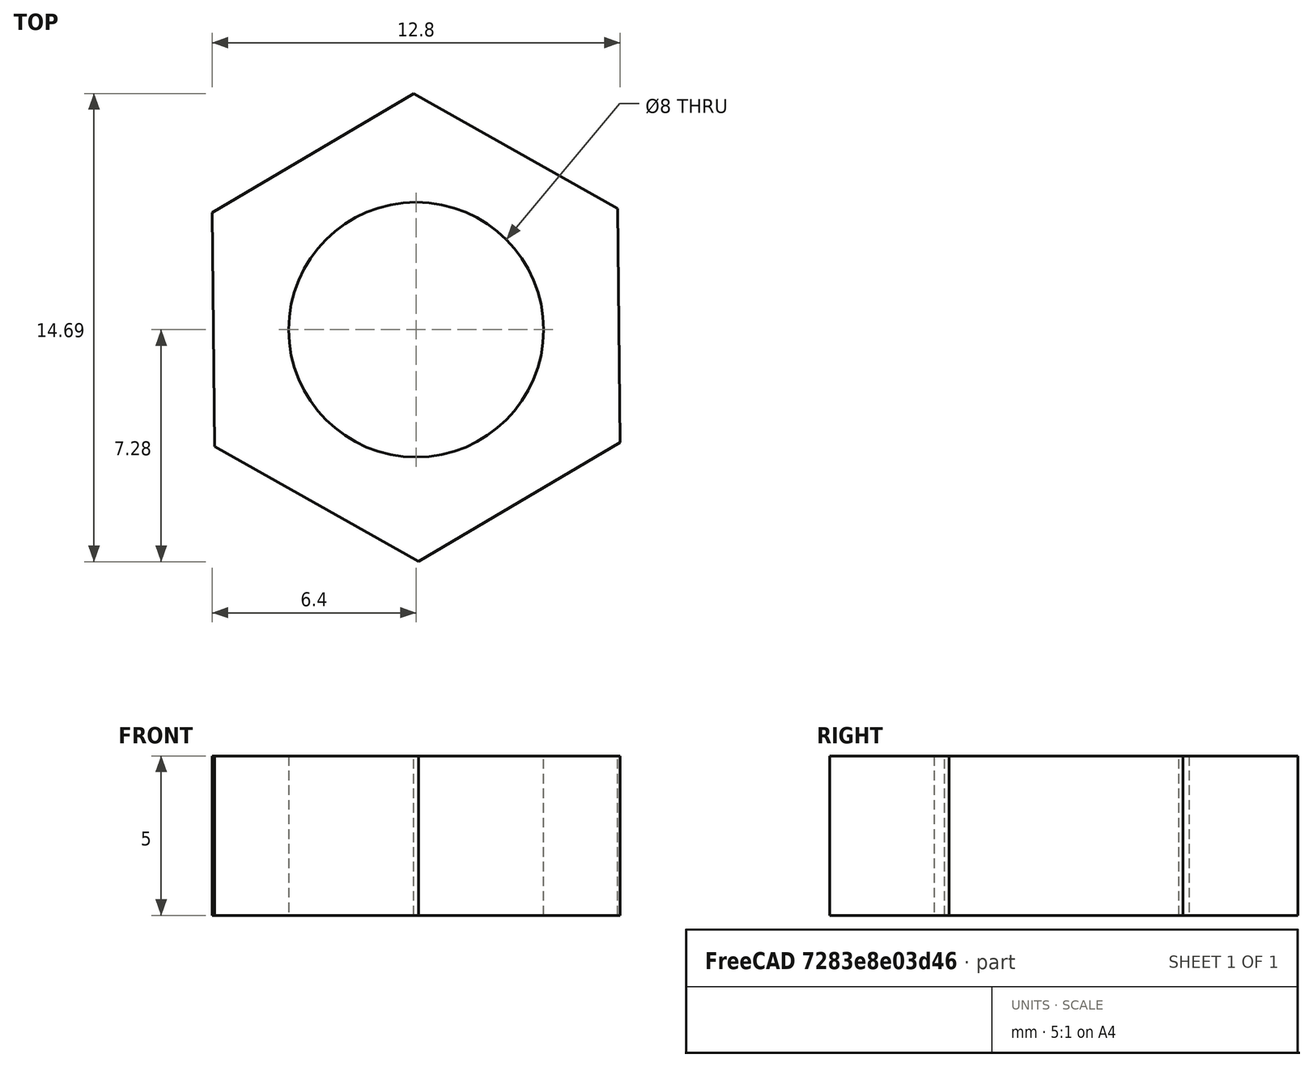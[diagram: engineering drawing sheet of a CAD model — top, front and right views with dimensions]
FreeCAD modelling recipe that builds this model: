
FCSTD DOCUMENT  (FreeCAD 0.19R24276 (Git))
Label: M8x5_gaika_1
License: All rights reserved
LicenseURL: http://en.wikipedia.org/wiki/All_rights_reserved
objects: Sketcher::SketchObject×1, PartDesign::Pad×1, PartDesign::Body×1
note: 4 computed .brp shape members not serialized (recipe doc carries the construction recipe); baked Part::Feature solids carry a one-line shape summary decoded from their .brp

FEATURE [Sketcher::SketchObject] Sketch
  FullyConstrained = false
  MapMode = 5
  Support = -> [XY_Plane]
  sketch-geometry (7):
    g0: Circle CenterX=0 CenterY=0 CenterZ=0 NormalX=0 NormalY=0 NormalZ=1 AngleXU=0 Radius=4
    g1: LineSegment StartX=0.07611 StartY=-7.27787 StartZ=0 EndX=6.39869 EndY=-3.53964 EndZ=0
    g2: LineSegment StartX=6.39869 StartY=-3.53964 StartZ=0 EndX=6.32258 EndY=3.80499 EndZ=0
    g3: LineSegment StartX=6.32258 StartY=3.80499 StartZ=0 EndX=-0.07611 EndY=7.41139 EndZ=0
    g4: LineSegment StartX=-0.07611 StartY=7.41139 StartZ=0 EndX=-6.39869 EndY=3.67316 EndZ=0
    g5: LineSegment StartX=-6.39869 StartY=3.67316 StartZ=0 EndX=-6.32258 EndY=-3.67147 EndZ=0
    g6: LineSegment StartX=-6.32258 StartY=-3.67147 StartZ=0 EndX=0.07611 EndY=-7.27787 EndZ=0
  constraints (9):
    c: Coincident(g0,g-1)
    c: Diameter(g0) = 8
    c: Coincident(g1,g2)
    c: Coincident(g2,g3)
    c: Coincident(g3,g4)
    c: Coincident(g4,g5)
    c: Coincident(g5,g6)
    c: Coincident(g6,g1)
    c: Equal(g1, g2-g6) x5
FEATURE [PartDesign::Pad] Pad
  Direction = (1,1,1)
  Length = 5
  Length2 = 100
  Profile = -> Sketch
  Type = 0
FEATURE [PartDesign::Body] Body
  Group = -> [Sketch,Pad]
  Origin = -> Origin
  Tip = -> Pad
